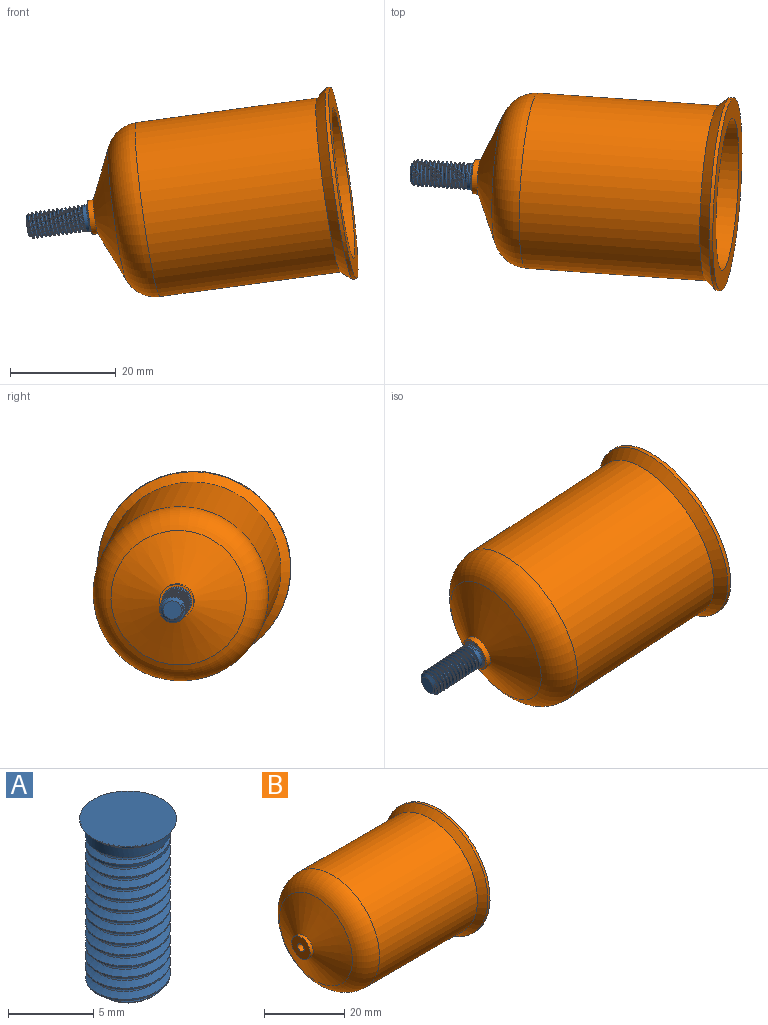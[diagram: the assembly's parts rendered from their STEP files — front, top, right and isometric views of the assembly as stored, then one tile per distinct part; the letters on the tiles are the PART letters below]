
ASSEMBLY  parts=2 mates=1
PART A: 27 faces, bbox 6.5x6.5x12 mm
  f0: bspline ~6.19x5.82mm, area 3.5mm2, adj f1,f3,f19
  f1: bspline ~5.25x5.15mm, area 3.5mm2, adj f0,f2,f4,f6,f19
  f2: bspline ~6.19x5.82mm, area 3.5mm2, adj f1,f5,f6
  f3: bspline ~10.54x5.01mm, area 91.8mm2, adj f0,f4,f6,f7,f8,f9,f10,f11
  f4: bspline ~10.49x4.13mm, area 39.6mm2, adj f1,f3,f5,f24
  f5: bspline ~10.33x5mm, area 87.5mm2, adj f2,f4,f7,f8,f9,f10,f11,f12
  f6: cylinder r=2.5mm len=5mm, axis (0,0,-1), area 3.7mm2, adj f1,f2,f3,f7,f19
  f7: cylinder r=2.5mm len=5mm, axis (0,0,-1), area 1.6mm2, adj f3,f5,f6,f8
  f8: cylinder r=2.5mm len=5mm, axis (0,0,-1), area 1.6mm2, adj f3,f5,f7,f9
  f9: cylinder r=2.5mm len=5mm, axis (0,0,-1), area 1.6mm2, adj f3,f5,f8,f10
  f10: cylinder r=2.5mm len=5mm, axis (0,0,-1), area 1.6mm2, adj f3,f5,f9,f11
  f11: cylinder r=2.5mm len=5mm, axis (0,0,-1), area 1.6mm2, adj f3,f5,f10,f12
  f12: cylinder r=2.5mm len=5mm, axis (0,0,-1), area 1.6mm2, adj f3,f5,f11,f13
  f13: cylinder r=2.5mm len=5mm, axis (0,0,-1), area 1.6mm2, adj f3,f5,f12,f14
  f14: cylinder r=2.5mm len=5mm, axis (0,0,-1), area 1.6mm2, adj f3,f5,f13,f15
  f15: cylinder r=2.5mm len=5mm, axis (0,0,-1), area 1.6mm2, adj f3,f5,f14,f16
  f16: cylinder r=2.5mm len=5mm, axis (0,0,-1), area 1.6mm2, adj f3,f5,f15,f17
  f17: cylinder r=2.5mm len=5mm, axis (0,0,-1), area 1.6mm2, adj f3,f5,f16,f18
  f18: cylinder r=2.5mm len=5mm, axis (0,0,-1), area 1.2mm2, adj f3,f5,f17,f23
  f19: cylinder r=2.5mm len=5mm, axis (0,0,-1), area 9.2mm2, adj f0,f1,f6,f22
  f20: torus R=2.85mm, axis (0,0,-1), area 2.6mm2, adj f21,f26
  f21: cone r=2.64mm half-angle=47deg, axis (0,0,1), area 3.4mm2, adj f20,f22
  f22: torus R=2.7mm, axis (0,0,-1), area 2.6mm2, adj f19,f21
  f23: cone r=2.12mm half-angle=50deg, axis (0,0,1), area 0.6mm2, adj f3,f5,f18,f24
  f24: cone r=2.12mm half-angle=50deg, axis (0,0,1), area 7.7mm2, adj f4,f5,f23,f25
  f25: plane 3.5x3.5mm, normal (0,0,-1), area 9.6mm2, adj f24
  f26: plane 5.7x5.7mm, normal (0,0,1), area 25.5mm2, adj f20
PART B: 14 faces, bbox 48.4x36.6x36.6 mm
  f0: cylinder r=14.42mm len=28.83mm, axis (-1,0,0), area 2575.2mm2, adj f1,f13
  f1: plane 36.59x36.59mm, normal (1,0,0), area 398.4mm2, adj f0,f2
  f2: cylinder r=18.29mm len=36.59mm, axis (-1,0,0), area 82.9mm2, adj f1,f3
  f3: cone r=18.29mm half-angle=39.9deg, axis (1,0,0), area 289.7mm2, adj f2,f4
  f4: cylinder r=16.6mm len=34.52mm, axis (-1,0,0), area 3599.4mm2, adj f3,f5
  f5: torus R=10.25mm, axis (-1,0,0), area 702.7mm2, adj f4,f6
  f6: cone r=3.24mm half-angle=66deg, axis (1,0,0), area 529.4mm2, adj f5,f7
  f7: cylinder r=3.24mm len=6.48mm, axis (-1,0,0), area 22mm2, adj f6,f8
  f8: plane 6.48x6.48mm, normal (-1,0,0), area 29mm2, adj f7,f9
  f9: cylinder r=1.13mm len=3.65mm, axis (-1,0,0), area 25.8mm2, adj f8,f10
  f10: cone r=5.08mm half-angle=63.6deg, axis (1,0,0), area 86.1mm2, adj f9,f11
  f11: cylinder r=5.08mm len=10.16mm, axis (-1,0,0), area 202.7mm2, adj f10,f12
  f12: cone r=5.08mm half-angle=68.4deg, axis (1,0,0), area 279mm2, adj f11,f13
  f13: torus R=8.07mm, axis (-1,0,0), area 619.4mm2, adj f0,f12
PLACE A rot(axis=(0.6,0.48,0.64),118deg) t=(-34.18,-1.1,23.33)mm
PLACE B rot(axis=(0.65,-0.7,-0.3),11.4deg) t=(-19.88,-2.09,25.27)mm
MATE fastened A.f21 <-> B.f0  axis (0.99,-0.07,0.13) through (-34.18,-1.1,23.33)mm
